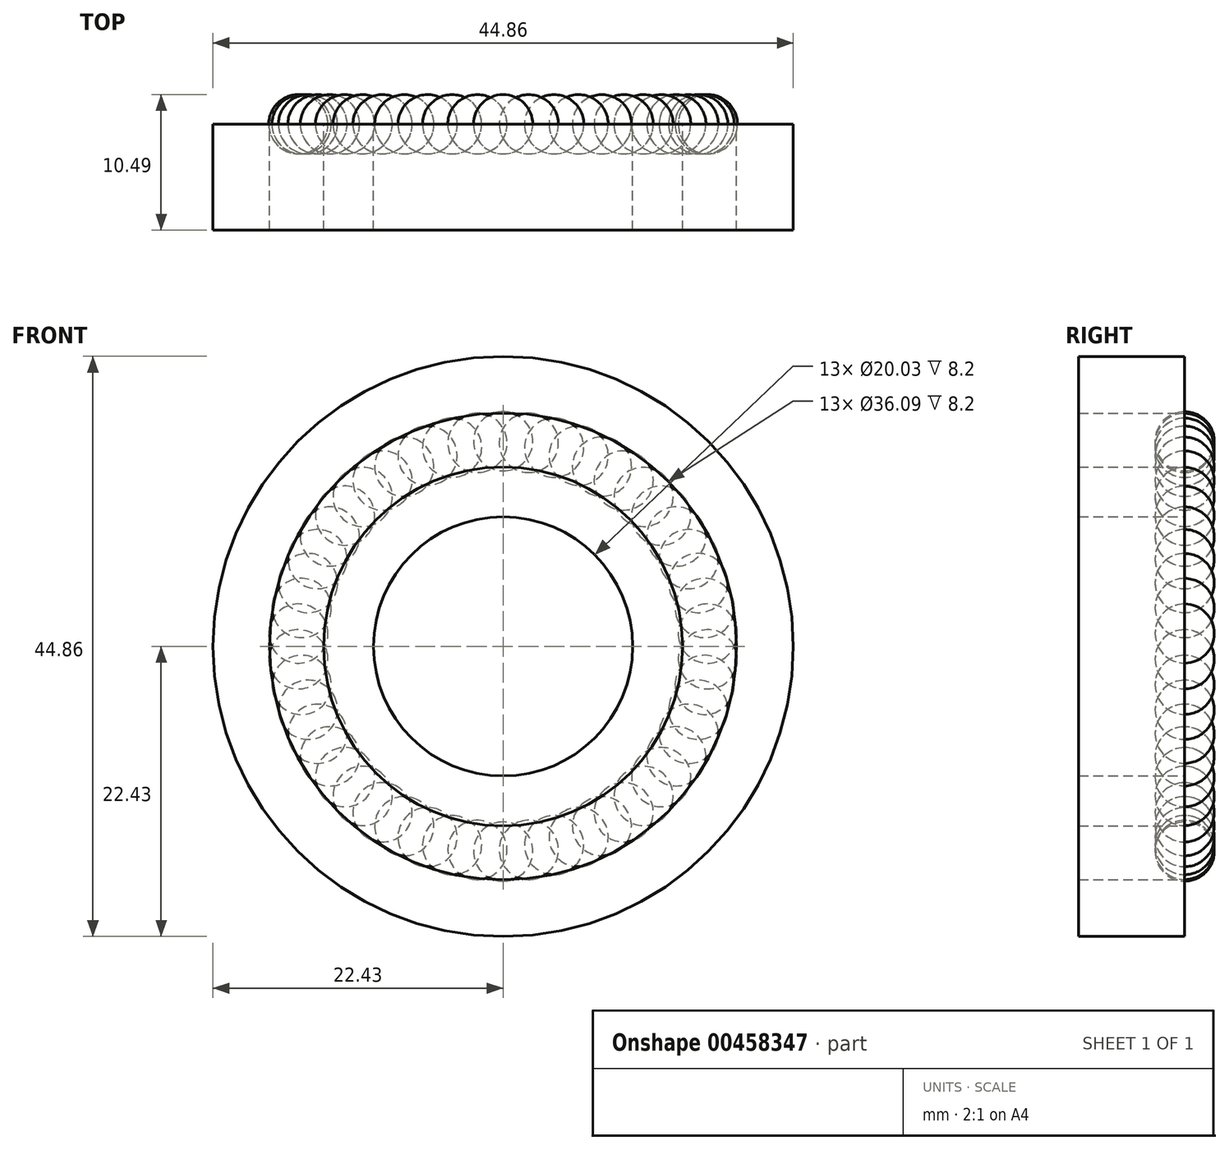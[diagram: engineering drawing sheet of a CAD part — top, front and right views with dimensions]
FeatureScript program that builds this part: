
annotation { "Feature Type Name" : "Feature", "Feature Type Description" : "" }
export const myFeature = defineFeature(function(context is Context, id is Id, definition is map)
    precondition{}
    {
        {
            var Q0;
            Q0=qCreatedBy(makeId("Front.planeOp"),FACE);
            var sketch = newSketch(context, id + "F0", { "sketchPlane" : qUnion([Q0])});
            skCircle(sketch, "E0", {"center": v(0, 0) * mm, "radius": 13.87 * mm});
            skCircle(sketch, "E1", {"center": v(0, 0) * mm, "radius": 10.02 * mm});
            skCircle(sketch, "E2", {"center": v(0, 0) * mm, "radius": 22.43 * mm});
            skCircle(sketch, "E3", {"center": v(0, 0) * mm, "radius": 18.04 * mm});
            skSolve(sketch);
        }
        {
            var Q0;
            Q0=makeQuery(id+"F0.imprint","IMPRINT",FACE,{"disambiguationData":[TD([[makeQuery(id+"F0.imprint","IMPRINT",EDGE,{"derivedFrom":sQuery(id+"F0.wireOp",EDGE,"E2")}),1.0]])]});
            var Q1;
            Q1=makeQuery(id+"F0.imprint","IMPRINT",FACE,{"disambiguationData":[TD([[makeQuery(id+"F0.imprint","IMPRINT",EDGE,{"derivedFrom":sQuery(id+"F0.wireOp",EDGE,"E0")}),1.0]])]});
            extrude(context, id + "F1", {"entities" : qUnion([Q0, Q1]), "depth" : 8.2 * mm});
        }
        {
            var Q0;
            Q0=qCreatedBy(makeId("Front.planeOp"),FACE);
            var sketch = newSketch(context, id + "F2", { "sketchPlane" : qUnion([Q0])});
            skLineSegment(sketch, "E4", {"start": v(0, 55.97) * mm, "end": v(0, -46.13) * mm});
            skCircle(sketch, "E5", {"center": v(0, 15.86) * mm, "radius": 2.29 * mm});
            skSolve(sketch);
        }
        {
            var Q0;
            {var subQ0=sQuery(id+"F2.wireOp",EDGE,"E5");var subQ1=sQuery(id+"F2.wireOp",EDGE,"E4");var subQ2=makeQuery(id+"F2.imprint","INTERSECT",VERTEX,{"disambiguationData":[OD(0.0)],"derivedFrom":[subQ1,subQ0]});Q0=makeQuery(id+"F2.imprint","IMPRINT",FACE,{"disambiguationData":[TD([[makeQuery(id+"F2.imprint","IMPRINT",EDGE,{"disambiguationData":[TD([[subQ2,1.0]])],"derivedFrom":subQ1}),1.0]])]});}
            var Q1;
            Q1=sQuery(id+"F2.wireOp",EDGE,"E4");
            revolve(context, id + "F3", {"entities" : qUnion([Q0]), "axis" : qUnion([Q1]), "revolveType" : RevolveType.FULL});
        }
        {
            var Q0;
            Q0=makeQuery(id+"F3.opRevolve","SWEPT_BODY",BODY,{"disambiguationData":[OSD([sQuery(id+"F2.wireOp",EDGE,"E4"),sQuery(id+"F2.wireOp",EDGE,"E5")])]});
            var Q1;
            Q1=makeQuery(id+"F1.opExtrude","SWEPT_FACE",FACE,{"disambiguationData":[OSD([sQuery(id+"F0.wireOp",EDGE,"E0")])]});
            circularPattern(context, id + "F4", {"entities" : qUnion([Q0]), "axis" : qUnion([Q1]), "angle" : 360 * degree, "instanceCount" : 50, "oppositeDirection" : true, "equalSpace" : true});
        }
    });
